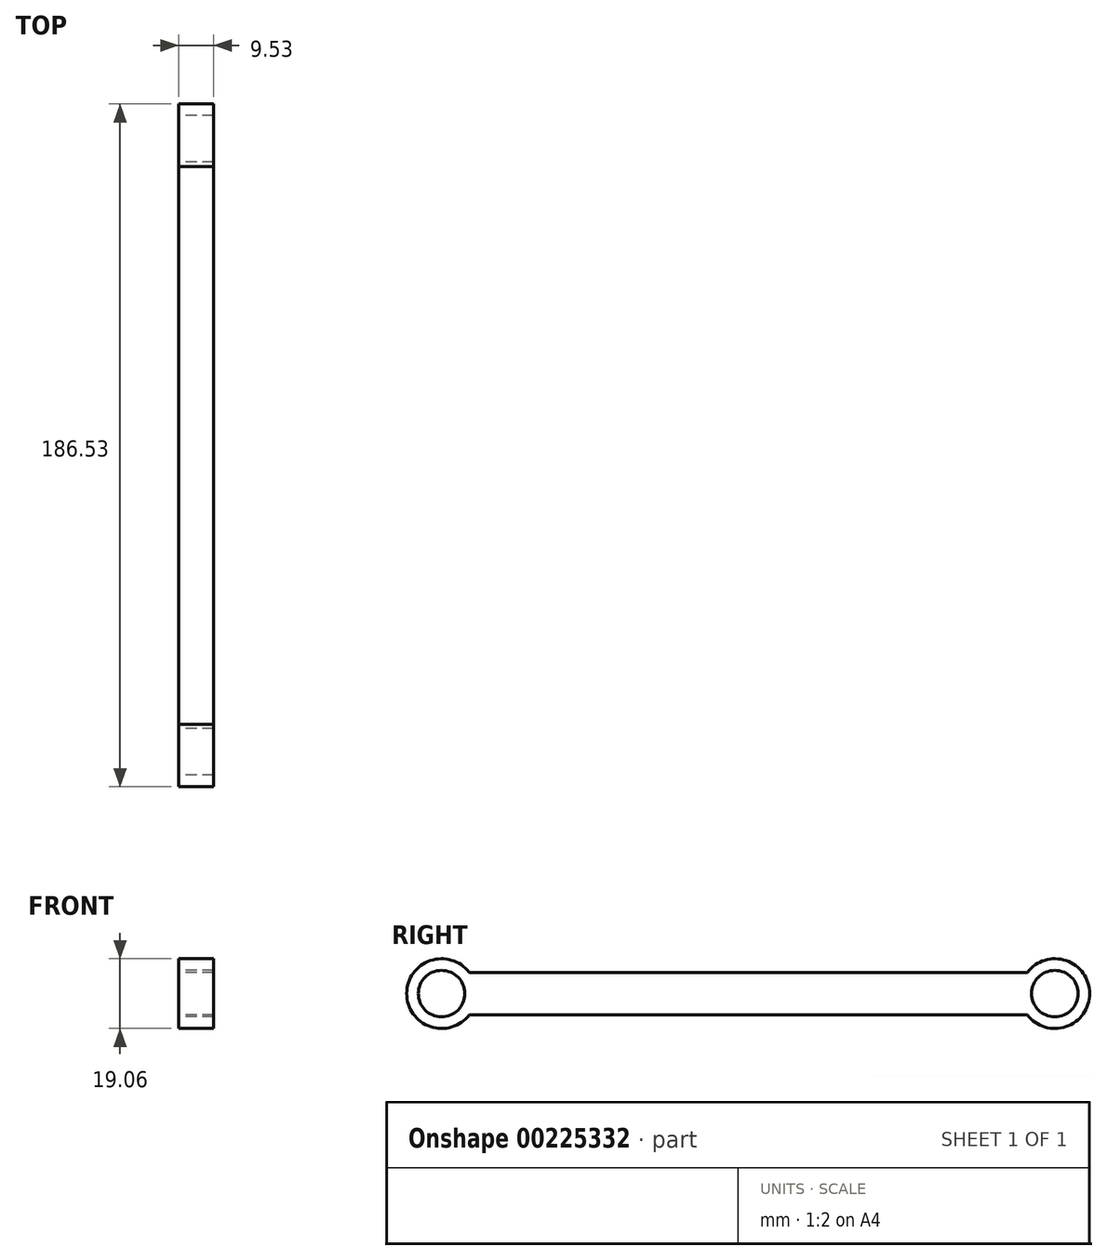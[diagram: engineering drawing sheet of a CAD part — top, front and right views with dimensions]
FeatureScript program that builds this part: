
annotation { "Feature Type Name" : "Feature", "Feature Type Description" : "" }
export const myFeature = defineFeature(function(context is Context, id is Id, definition is map)
    precondition{}
    {
        {
            var Q0;
            Q0=qCreatedBy(makeId("Right.planeOp"),FACE);
            var sketch = newSketch(context, id + "F0", { "sketchPlane" : qUnion([Q0])});
            skCircle(sketch, "E0", {"center": v(0, 0) * mm, "radius": 6.35 * mm});
            skCircle(sketch, "E1", {"center": v(167.49, 0) * mm, "radius": 6.35 * mm});
            skLineSegment(sketch, "E2.0", {"start": v(7.54, -5.82) * mm, "end": v(159.94, -5.82) * mm});
            skLineSegment(sketch, "E3.0", {"start": v(7.54, 5.82) * mm, "end": v(159.94, 5.82) * mm});
            skArc(sketch, "E4", {"start": v(7.54, 5.82) * mm, "mid": v(-9.53, 0) * mm, "end": v(7.54, -5.82) * mm});
            skArc(sketch, "E5", {"start": v(159.94, -5.82) * mm, "mid": v(177.01, 0) * mm, "end": v(159.94, 5.82) * mm});
            skLineSegment(sketch, "E6.trimOffspring", {"start": v(150.06, 5.82) * mm, "end": v(159.94, 5.82) * mm});
            skLineSegment(sketch, "E7.trimOffspring", {"start": v(162.6, -5.82) * mm, "end": v(164.94, -5.82) * mm});
            skSolve(sketch);
        }
        {
            var Q0;
            Q0 = qSketchRegion(id + "F0", true);
            extrude(context, id + "F1", {"entities" : qUnion([Q0]), "depth" : 9.52 * mm});
        }
    });
